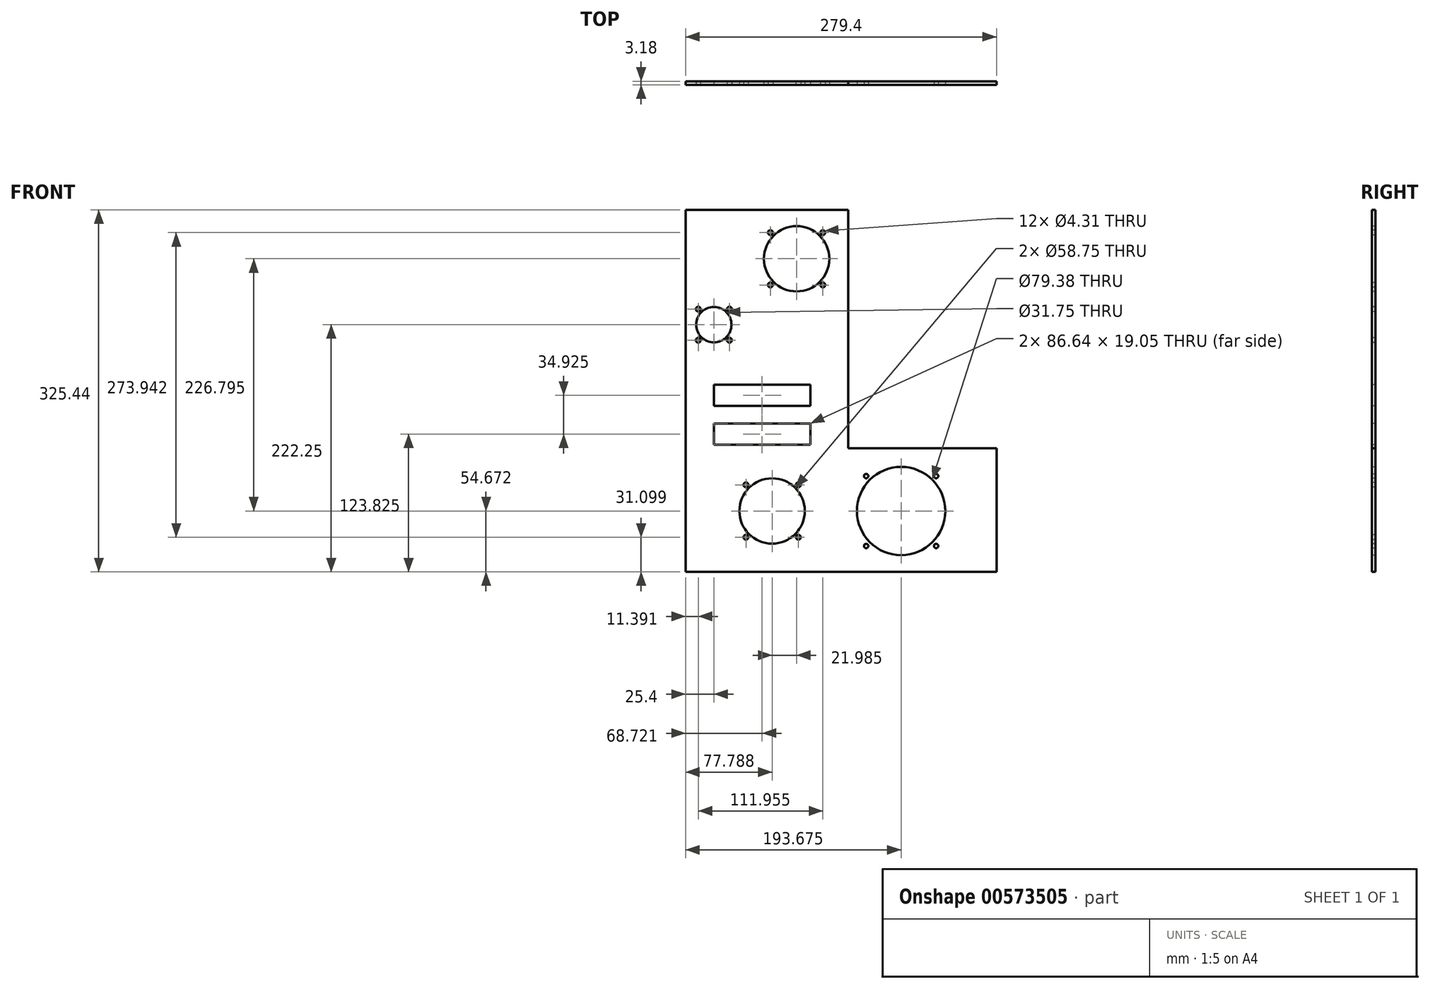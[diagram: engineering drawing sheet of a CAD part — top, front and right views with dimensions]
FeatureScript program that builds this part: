
annotation { "Feature Type Name" : "Feature", "Feature Type Description" : "" }
export const myFeature = defineFeature(function(context is Context, id is Id, definition is map)
    precondition{}
    {
        {
            var Q0;
            Q0=qCreatedBy(makeId("Front.planeOp"),FACE);
            var sketch = newSketch(context, id + "F0", { "sketchPlane" : qUnion([Q0])});
            skLineSegment(sketch, "E0", {"start": v(0, 325.44) * mm, "end": v(0, 0) * mm});
            skLineSegment(sketch, "E1", {"start": v(0, 0) * mm, "end": v(279.4, 0) * mm});
            skLineSegment(sketch, "E2", {"start": v(279.4, 0) * mm, "end": v(279.4, 111.13) * mm});
            skLineSegment(sketch, "E3", {"start": v(279.4, 111.13) * mm, "end": v(146.05, 111.13) * mm});
            skLineSegment(sketch, "E4", {"start": v(146.05, 111.12) * mm, "end": v(146.05, 325.44) * mm});
            skLineSegment(sketch, "E5", {"start": v(146.05, 325.44) * mm, "end": v(0, 325.44) * mm});
            skSolve(sketch);
        }
        {
            var Q0;
            Q0=makeQuery(id+"F0.imprint","IMPRINT",FACE,{"disambiguationData":[TD([[makeQuery(id+"F0.imprint","IMPRINT",EDGE,{"derivedFrom":sQuery(id+"F0.wireOp",EDGE,"E0")}),1.0]])]});
            extrude(context, id + "F1", {"entities" : qUnion([Q0]), "depth" : 3.17 * mm, "offsetDistance" : 25.4 * mm});
        }
        {
            var Q0;
            Q0=makeQuery(id+"F1.opExtrude","CAP_FACE",FACE,{"disambiguationData":[OSD([sQuery(id+"F0.wireOp",EDGE,"E0"),sQuery(id+"F0.wireOp",EDGE,"E1"),sQuery(id+"F0.wireOp",EDGE,"E2"),sQuery(id+"F0.wireOp",EDGE,"E3"),sQuery(id+"F0.wireOp",EDGE,"E4"),sQuery(id+"F0.wireOp",EDGE,"E5")])],"isStart":false});
            var sketch = newSketch(context, id + "F2", { "sketchPlane" : qUnion([Q0])});
            skCircle(sketch, "E6", {"center": v(193.68, 54.67) * mm, "radius": 39.69 * mm});
            skCircle(sketch, "E7.0.1.0", {"center": v(162.24, 86.1) * mm, "radius": 1.96 * mm});
            skCircle(sketch, "E7.0.1.1", {"center": v(225.1, 86.1) * mm, "radius": 1.96 * mm});
            skCircle(sketch, "E7.0.1.2", {"center": v(225.1, 23.24) * mm, "radius": 1.96 * mm});
            skCircle(sketch, "E7.0.1.3", {"center": v(162.24, 23.24) * mm, "radius": 1.96 * mm});
            skLineSegment(sketch, "E8", {"start": v(162.24, 86.1) * mm, "end": v(225.1, 23.24) * mm});
            skLineSegment(sketch, "E9", {"start": v(225.1, 86.1) * mm, "end": v(162.24, 23.24) * mm});
            skCircle(sketch, "E10", {"center": v(25.4, 222.25) * mm, "radius": 15.88 * mm});
            skCircle(sketch, "E11", {"center": v(11.4, 236.26) * mm, "radius": 2.15 * mm});
            skCircle(sketch, "E12", {"center": v(39.4, 236.26) * mm, "radius": 2.15 * mm});
            skCircle(sketch, "E13", {"center": v(39.4, 208.24) * mm, "radius": 2.15 * mm});
            skCircle(sketch, "E14", {"center": v(11.4, 208.24) * mm, "radius": 2.15 * mm});
            skCircle(sketch, "E15", {"center": v(99.77, 281.47) * mm, "radius": 29.38 * mm});
            skCircle(sketch, "E16", {"center": v(76.2, 305.04) * mm, "radius": 2.15 * mm});
            skCircle(sketch, "E17", {"center": v(123.35, 305.04) * mm, "radius": 2.15 * mm});
            skCircle(sketch, "E18", {"center": v(123.35, 257.9) * mm, "radius": 2.15 * mm});
            skCircle(sketch, "E19", {"center": v(76.2, 257.9) * mm, "radius": 2.15 * mm});
            skLineSegment(sketch, "E20", {"start": v(76.2, 305.04) * mm, "end": v(123.35, 257.9) * mm});
            skLineSegment(sketch, "E21", {"start": v(123.35, 305.04) * mm, "end": v(76.2, 257.9) * mm});
            skLineSegment(sketch, "E22", {"start": v(11.4, 236.26) * mm, "end": v(39.4, 208.24) * mm});
            skLineSegment(sketch, "E23", {"start": v(39.4, 236.26) * mm, "end": v(11.4, 208.24) * mm});
            skLineSegment(sketch, "E24.bottom", {"start": v(25.4, 168.28) * mm, "end": v(112.04, 168.28) * mm});
            skLineSegment(sketch, "E24.top", {"start": v(25.4, 149.23) * mm, "end": v(112.04, 149.23) * mm});
            skLineSegment(sketch, "E24.left", {"start": v(25.4, 168.28) * mm, "end": v(25.4, 149.23) * mm});
            skLineSegment(sketch, "E24.right", {"start": v(112.04, 168.28) * mm, "end": v(112.04, 149.23) * mm});
            skLineSegment(sketch, "E25.bottom", {"start": v(25.4, 133.35) * mm, "end": v(112.04, 133.35) * mm});
            skLineSegment(sketch, "E25.top", {"start": v(25.4, 114.3) * mm, "end": v(112.04, 114.3) * mm});
            skLineSegment(sketch, "E25.left", {"start": v(25.4, 133.35) * mm, "end": v(25.4, 114.3) * mm});
            skLineSegment(sketch, "E25.right", {"start": v(112.04, 133.35) * mm, "end": v(112.04, 114.3) * mm});
            skCircle(sketch, "E26", {"center": v(77.79, 54.67) * mm, "radius": 29.38 * mm});
            skCircle(sketch, "E27", {"center": v(54.21, 78.25) * mm, "radius": 2.15 * mm});
            skCircle(sketch, "E28", {"center": v(101.36, 78.25) * mm, "radius": 2.15 * mm});
            skCircle(sketch, "E29", {"center": v(101.36, 31.1) * mm, "radius": 2.15 * mm});
            skCircle(sketch, "E30", {"center": v(54.21, 31.1) * mm, "radius": 2.15 * mm});
            skLineSegment(sketch, "E31", {"start": v(54.21, 78.25) * mm, "end": v(101.36, 31.1) * mm});
            skLineSegment(sketch, "E32", {"start": v(101.36, 78.25) * mm, "end": v(54.21, 31.1) * mm});
            skSolve(sketch);
        }
        {
            var Q0;
            Q0 = qSketchRegion(id + "F2", true);
            extrude(context, id + "F3", {"entities" : qUnion([Q0]), "operationType" : NewBodyOperationType.REMOVE, "oppositeDirection" : true, "depth" : 25.4 * mm, "offsetDistance" : 25.4 * mm});
        }
    });
